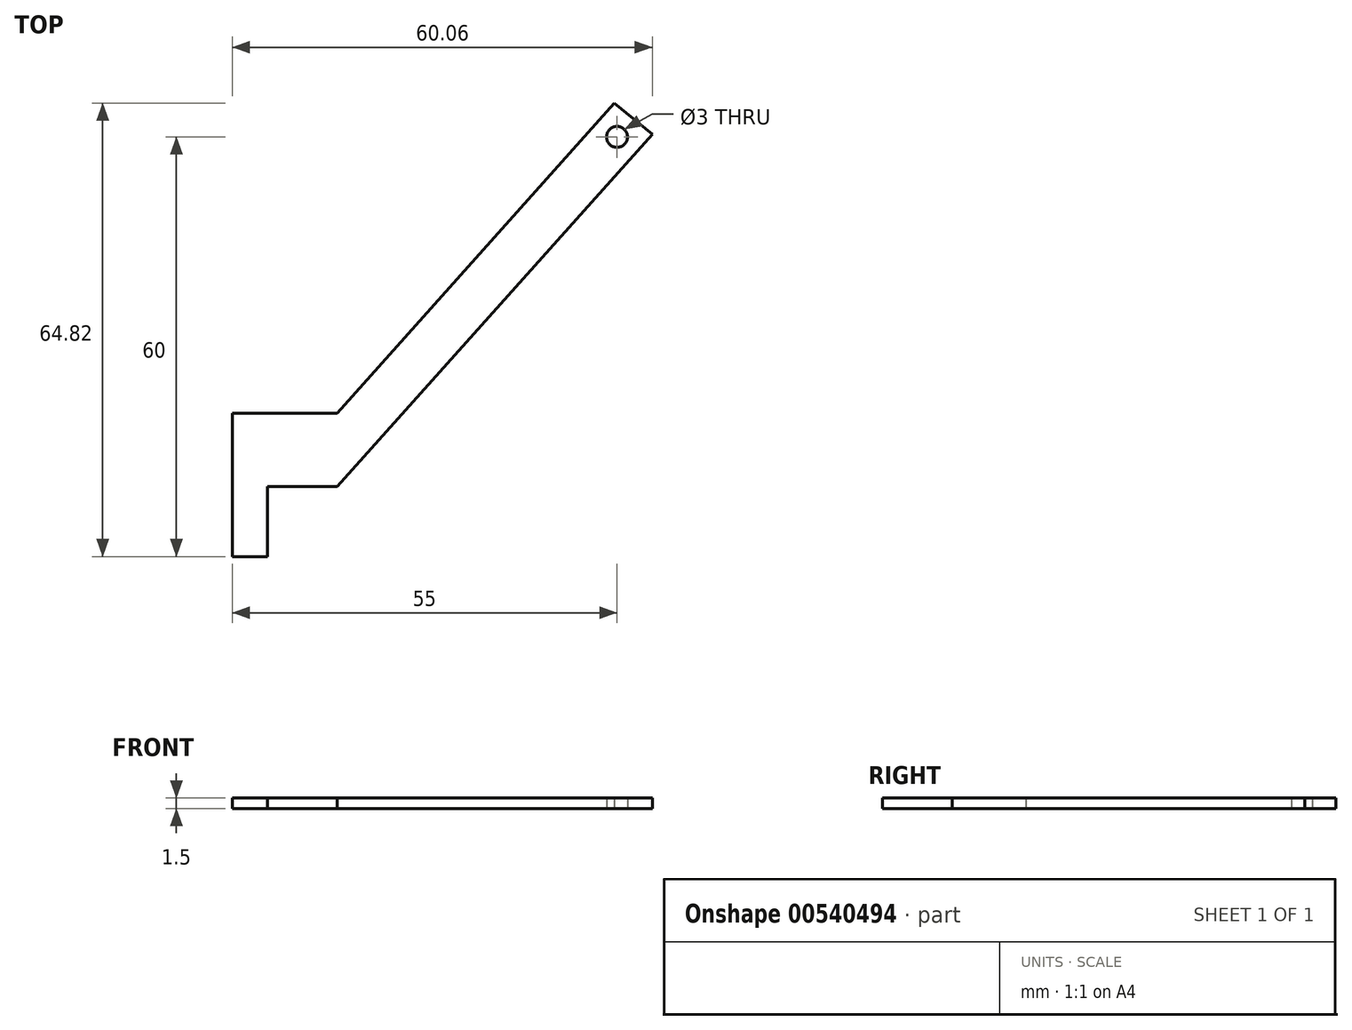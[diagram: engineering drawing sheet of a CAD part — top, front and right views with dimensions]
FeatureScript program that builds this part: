
annotation { "Feature Type Name" : "Feature", "Feature Type Description" : "" }
export const myFeature = defineFeature(function(context is Context, id is Id, definition is map)
    precondition{}
    {
        {
            var Q0;
            Q0=qCreatedBy(makeId("Top.planeOp"),FACE);
            var sketch = newSketch(context, id + "F0", { "sketchPlane" : qUnion([Q0])});
            skCircle(sketch, "E0", {"center": v(55, 60) * mm, "radius": 1.5 * mm});
            skLineSegment(sketch, "E1", {"start": v(0, 0) * mm, "end": v(5, 0) * mm});
            skLineSegment(sketch, "E2", {"start": v(5, 0) * mm, "end": v(5, 10) * mm});
            skLineSegment(sketch, "E3", {"start": v(5, 10) * mm, "end": v(15, 10) * mm});
            skLineSegment(sketch, "E4", {"start": v(15, 10) * mm, "end": v(60.06, 60.4) * mm});
            skLineSegment(sketch, "E5", {"start": v(60.06, 60.4) * mm, "end": v(54.61, 64.82) * mm});
            skLineSegment(sketch, "E6", {"start": v(54.61, 64.82) * mm, "end": v(15, 20.5) * mm});
            skLineSegment(sketch, "E7", {"start": v(15, 20.5) * mm, "end": v(0, 20.5) * mm});
            skLineSegment(sketch, "E8", {"start": v(0, 20.5) * mm, "end": v(0, 0) * mm});
            skSolve(sketch);
        }
        {
            var Q0;
            Q0 = qSketchRegion(id + "F0", true);
            extrude(context, id + "F1", {"entities" : qUnion([Q0]), "depth" : (0.3 * 5) * mm, "offsetDistance" : 25 * mm});
        }
    });
